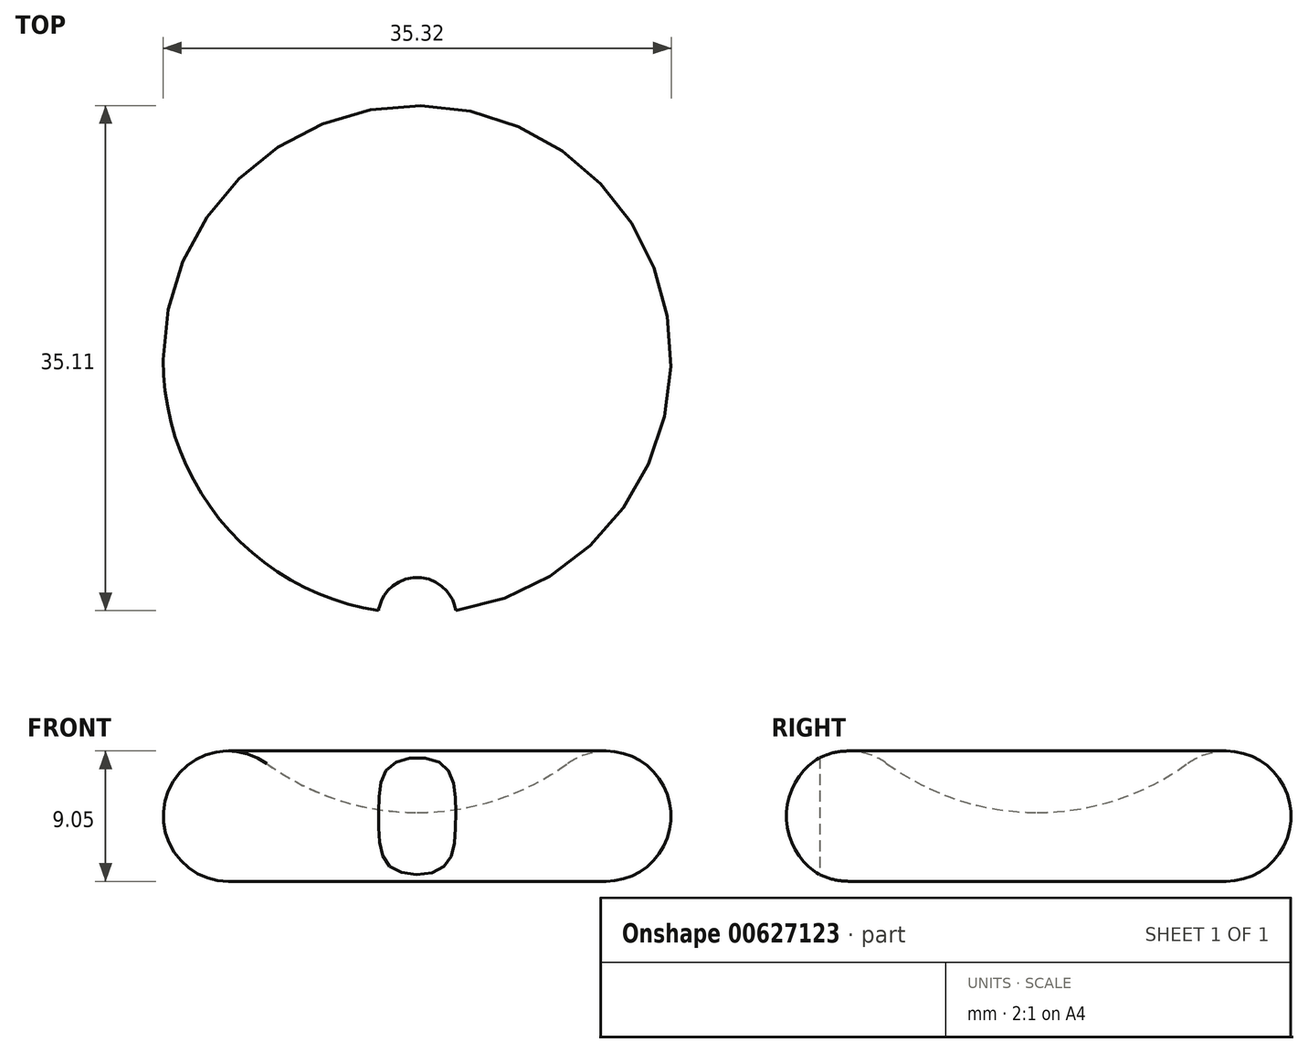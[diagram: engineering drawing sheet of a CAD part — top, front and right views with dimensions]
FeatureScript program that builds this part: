
annotation { "Feature Type Name" : "Feature", "Feature Type Description" : "" }
export const myFeature = defineFeature(function(context is Context, id is Id, definition is map)
    precondition{}
    {
        {
            var Q0;
            Q0=qCreatedBy(makeId("Front.planeOp"),FACE);
            var sketch = newSketch(context, id + "F0", { "sketchPlane" : qUnion([Q0])});
            skLineSegment(sketch, "E0", {"start": v(0, 0) * mm, "end": v(-13.62, 0) * mm});
            skCircle(sketch, "E1", {"center": v(-13.13, 4.53) * mm, "radius": 4.53 * mm});
            skCircle(sketch, "E2", {"center": v(0, 22.56) * mm, "radius": 17.79 * mm});
            skLineSegment(sketch, "E3", {"start": v(0, 0) * mm, "end": v(0, 4.78) * mm});
            skSolve(sketch);
        }
        {
            var Q0;
            {var subQ0=sQuery(id+"F0.wireOp",EDGE,"E3");Q0=makeQuery(id+"F0.imprint","IMPRINT",FACE,{"disambiguationData":[TD([[makeQuery(id+"F0.imprint","IMPRINT",EDGE,{"derivedFrom":subQ0}),1.0]])]});}
            var Q1;
            {var subQ0=sQuery(id+"F0.wireOp",EDGE,"E1");var subQ1=makeQuery(id+"F0.imprint","INTERSECT",VERTEX,{"derivedFrom":[sQuery(id+"F0.wireOp",EDGE,"E0"),subQ0]});Q1=makeQuery(id+"F0.imprint","IMPRINT",FACE,{"disambiguationData":[TD([[makeQuery(id+"F0.imprint","IMPRINT",EDGE,{"disambiguationData":[TD([[subQ1,1.0]])],"derivedFrom":subQ0}),1.0]])]});}
            var Q2;
            Q2=sQuery(id+"F0.wireOp",EDGE,"E3");
            revolve(context, id + "F1", {"entities" : qUnion([Q0, Q1]), "axis" : qUnion([Q2]), "revolveType" : RevolveType.FULL});
        }
        {
            var Q0;
            Q0=qCreatedBy(makeId("Top.planeOp"),FACE);
            var sketch = newSketch(context, id + "F2", { "sketchPlane" : qUnion([Q0])});
            skCircle(sketch, "E4", {"center": v(0, -17.85) * mm, "radius": 2.71 * mm});
            skSolve(sketch);
        }
        {
            var Q0;
            Q0=makeQuery(id+"F2.imprint","IMPRINT",FACE,{"disambiguationData":[TD([[makeQuery(id+"F2.imprint","IMPRINT",EDGE,{"derivedFrom":sQuery(id+"F2.wireOp",EDGE,"E4")}),1.0]])]});
            extrude(context, id + "F3", {"entities" : qUnion([Q0]), "operationType" : NewBodyOperationType.REMOVE, "depth" : 25 * mm, "offsetDistance" : 25 * mm});
        }
    });
